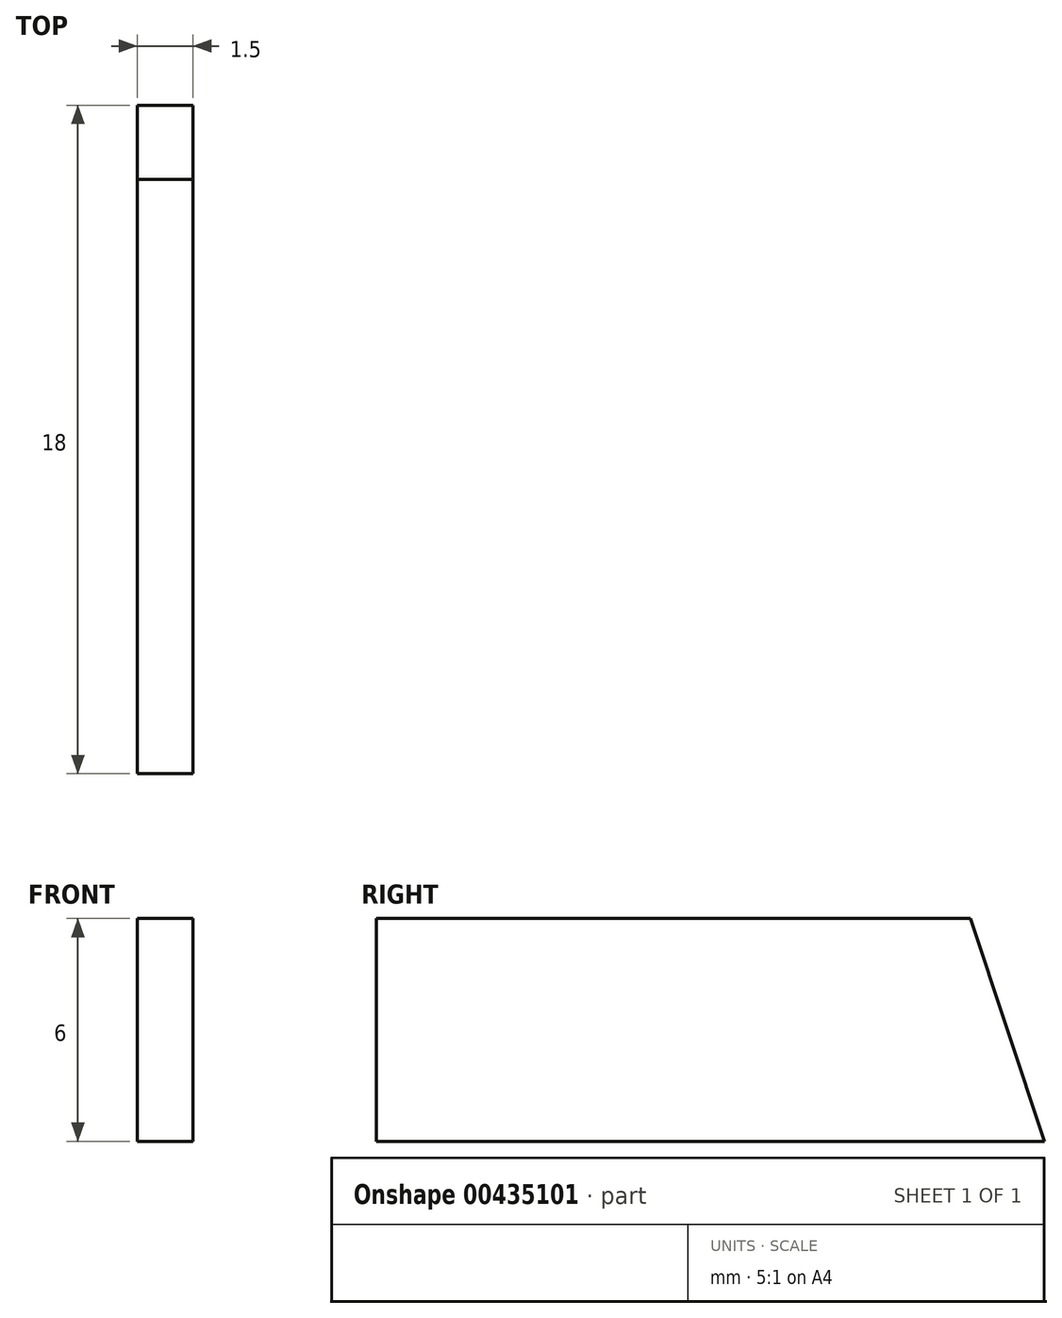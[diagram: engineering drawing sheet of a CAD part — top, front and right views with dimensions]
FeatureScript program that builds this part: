
annotation { "Feature Type Name" : "Feature", "Feature Type Description" : "" }
export const myFeature = defineFeature(function(context is Context, id is Id, definition is map)
    precondition{}
    {
        {
            var Q0;
            Q0=qCreatedBy(makeId("Right.planeOp"),FACE);
            var sketch = newSketch(context, id + "F0", { "sketchPlane" : qUnion([Q0])});
            skLineSegment(sketch, "E0", {"start": v(0, 0) * mm, "end": v(0, 6) * mm});
            skLineSegment(sketch, "E1", {"start": v(0, 6) * mm, "end": v(16, 6) * mm});
            skLineSegment(sketch, "E2", {"start": v(16, 6) * mm, "end": v(18, 0) * mm});
            skLineSegment(sketch, "E3", {"start": v(18, 0) * mm, "end": v(0, 0) * mm});
            skSolve(sketch);
        }
        {
            var Q0;
            Q0 = qSketchRegion(id + "F0", true);
            extrude(context, id + "F1", {"entities" : qUnion([Q0]), "depth" : 1.5 * mm});
        }
    });
